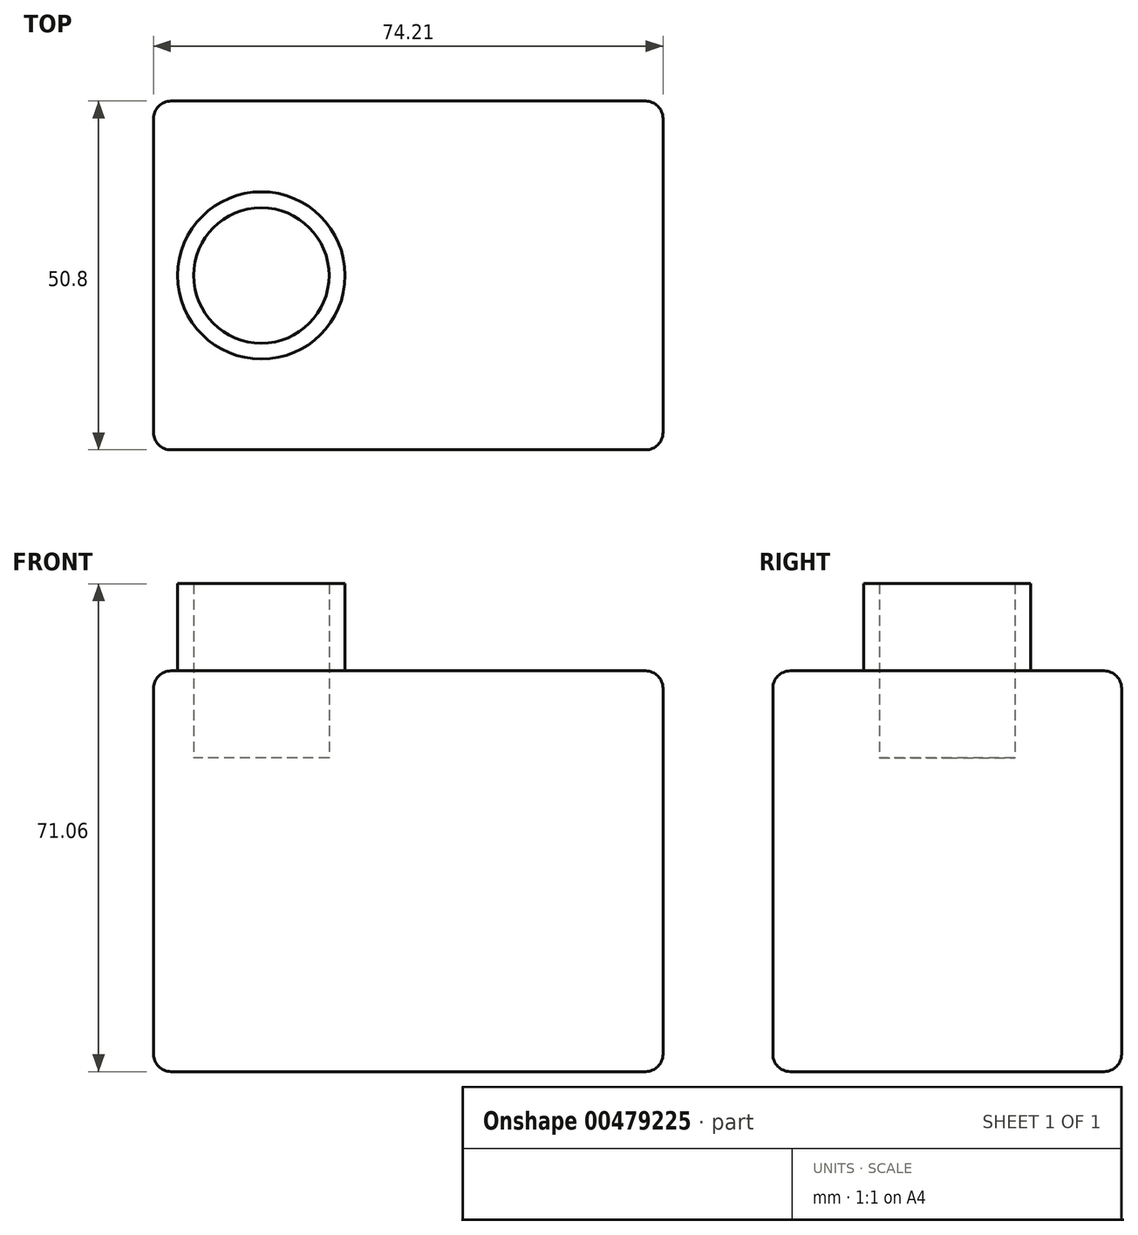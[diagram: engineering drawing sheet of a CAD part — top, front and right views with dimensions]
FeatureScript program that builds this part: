
annotation { "Feature Type Name" : "Feature", "Feature Type Description" : "" }
export const myFeature = defineFeature(function(context is Context, id is Id, definition is map)
    precondition{}
    {
        {
            var Q0;
            Q0=qCreatedBy(makeId("Front.planeOp"),FACE);
            var sketch = newSketch(context, id + "F0", { "sketchPlane" : qUnion([Q0])});
            skLineSegment(sketch, "E0.bottom", {"start": v(0, 0) * mm, "end": v(-74.21, 0) * mm});
            skLineSegment(sketch, "E0.top", {"start": v(0, 58.36) * mm, "end": v(-74.21, 58.36) * mm});
            skLineSegment(sketch, "E0.left", {"start": v(0, 0) * mm, "end": v(0, 58.36) * mm});
            skLineSegment(sketch, "E0.right", {"start": v(-74.21, 0) * mm, "end": v(-74.21, 58.36) * mm});
            skSolve(sketch);
        }
        {
            var Q0;
            Q0 = qSketchRegion(id + "F0", true);
            extrude(context, id + "F1", {"entities" : qUnion([Q0]), "endBound" : BoundingType.SYMMETRIC, "depth" : 50.8 * mm});
        }
        {
            var Q0;
            Q0=makeQuery(id+"F1.opExtrude","SWEPT_EDGE",EDGE,{"disambiguationData":[OSD([sQuery(id+"F0.wireOp",EDGE,"E0.top"),sQuery(id+"F0.wireOp",EDGE,"E0.right")])]});
            var Q1;
            Q1=makeQuery(id+"F1.opExtrude","CAP_EDGE",EDGE,{"disambiguationData":[OSD([sQuery(id+"F0.wireOp",EDGE,"E0.top")])],"isStart":false});
            var Q2;
            Q2=makeQuery(id+"F1.opExtrude","CAP_FACE",FACE,{"disambiguationData":[OSD([sQuery(id+"F0.wireOp",EDGE,"E0.bottom"),sQuery(id+"F0.wireOp",EDGE,"E0.top"),sQuery(id+"F0.wireOp",EDGE,"E0.left"),sQuery(id+"F0.wireOp",EDGE,"E0.right")])],"isStart":false});
            var Q3;
            Q3=makeQuery(id+"F1.opExtrude","SWEPT_EDGE",EDGE,{"disambiguationData":[OSD([sQuery(id+"F0.wireOp",EDGE,"E0.top"),sQuery(id+"F0.wireOp",EDGE,"E0.left")])]});
            var Q4;
            Q4=makeQuery(id+"F1.opExtrude","CAP_EDGE",EDGE,{"disambiguationData":[OSD([sQuery(id+"F0.wireOp",EDGE,"E0.top")])],"isStart":true});
            var Q5;
            Q5=makeQuery(id+"F1.opExtrude","CAP_FACE",FACE,{"disambiguationData":[OSD([sQuery(id+"F0.wireOp",EDGE,"E0.bottom"),sQuery(id+"F0.wireOp",EDGE,"E0.top"),sQuery(id+"F0.wireOp",EDGE,"E0.left"),sQuery(id+"F0.wireOp",EDGE,"E0.right")])],"isStart":true});
            var Q6;
            Q6=makeQuery(id+"F1.opExtrude","SWEPT_FACE",FACE,{"disambiguationData":[OSD([sQuery(id+"F0.wireOp",EDGE,"E0.right")])]});
            var Q7;
            Q7=makeQuery(id+"F1.opExtrude","SWEPT_FACE",FACE,{"disambiguationData":[OSD([sQuery(id+"F0.wireOp",EDGE,"E0.left")])]});
            fillet(context, id + "F2", {"entities" : qUnion([Q0, Q1, Q2, Q3, Q4, Q5, Q6, Q7]), "radius" : 2.54 * mm, "tangentPropagation" : true, "allowEdgeOverflow" : false});
        }
        {
            var Q0;
            Q0=makeQuery(id+"F1.opExtrude","SWEPT_FACE",FACE,{"disambiguationData":[OSD([sQuery(id+"F0.wireOp",EDGE,"E0.top")])]});
            var sketch = newSketch(context, id + "F3", { "sketchPlane" : qUnion([Q0])});
            skCircle(sketch, "E1", {"center": v(-58.5, 0) * mm, "radius": 12.19 * mm});
            skSolve(sketch);
        }
        {
            var Q0;
            Q0 = qSketchRegion(id + "F3", true);
            extrude(context, id + "F4", {"entities" : qUnion([Q0]), "operationType" : NewBodyOperationType.ADD, "depth" : 12.7 * mm});
        }
        {
            var Q0;
            Q0=makeQuery(id+"F1.opExtrude","SWEPT_FACE",FACE,{"disambiguationData":[OSD([sQuery(id+"F0.wireOp",EDGE,"E0.top")])]});
            var sketch = newSketch(context, id + "F5", { "sketchPlane" : qUnion([Q0])});
            skCircle(sketch, "E2", {"center": v(-58.5, 0) * mm, "radius": 9.86 * mm});
            skSolve(sketch);
        }
        {
            var Q0;
            Q0 = qSketchRegion(id + "F5", true);
            extrude(context, id + "F6", {"entities" : qUnion([Q0]), "operationType" : NewBodyOperationType.REMOVE, "endBound" : BoundingType.SYMMETRIC, "depth" : 25.4 * mm});
        }
    });
